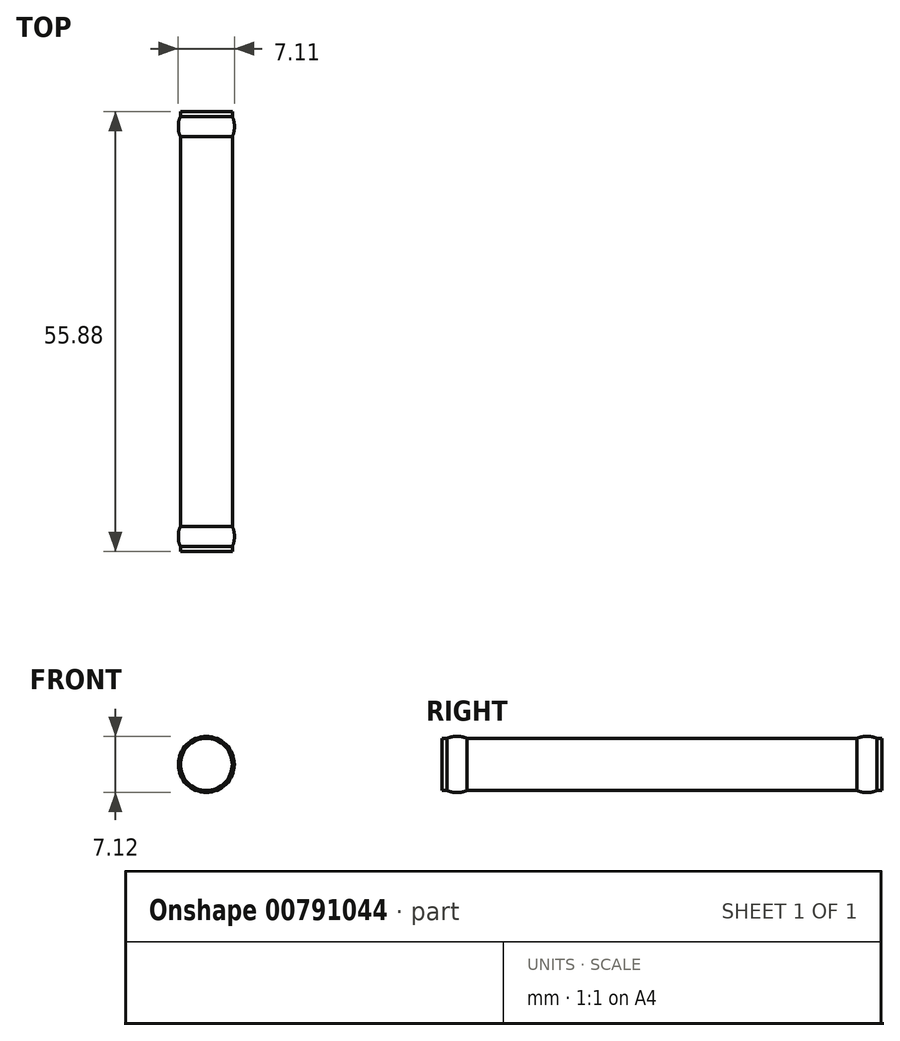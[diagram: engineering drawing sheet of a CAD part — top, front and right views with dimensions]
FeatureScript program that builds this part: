
annotation { "Feature Type Name" : "Feature", "Feature Type Description" : "" }
export const myFeature = defineFeature(function(context is Context, id is Id, definition is map)
    precondition{}
    {
        {
            var Q0;
            Q0=qCreatedBy(makeId("Front.planeOp"),FACE);
            var sketch = newSketch(context, id + "F0", { "sketchPlane" : qUnion([Q0])});
            skCircle(sketch, "E0", {"center": v(-16, 0) * mm, "radius": 3.3 * mm});
            skLineSegment(sketch, "E1", {"start": v(-12.7, 0) * mm, "end": v(0, 0) * mm});
            skSolve(sketch);
        }
        {
            var Q0;
            Q0=makeQuery(id+"F0.imprint","IMPRINT",FACE,{"disambiguationData":[TD([[makeQuery(id+"F0.imprint","IMPRINT",EDGE,{"derivedFrom":sQuery(id+"F0.wireOp",EDGE,"E0")}),1.0]])]});
            var Q1;
            Q1=makeQuery(id+"F0.imprint","IMPRINT",FACE,{"disambiguationData":[TD([[makeQuery(id+"F0.imprint","IMPRINT",EDGE,{"derivedFrom":sQuery(id+"F0.wireOp",EDGE,"TjowqyiQ-MTEW-wuyz-Xt5a-qvUKrSVn7oxo")}),1.0]])]});
            extrude(context, id + "F1", {"entities" : qUnion([Q0, Q1]), "depth" : 55.88 * mm, "offsetDistance" : 25.4 * mm});
        }
        {
            var Q0;
            Q0=makeQuery(id+"F1.opExtrude","CAP_FACE",FACE,{"disambiguationData":[OSD([sQuery(id+"F0.wireOp",EDGE,"E0")])],"isStart":false});
            cPlane(context, id + "F2", {"entities" : qUnion([Q0]), "cplaneType" : CPlaneType.OFFSET, "offset" : 1.9 * mm, "oppositeDirection" : true, "width" : 152.4 * mm, "height" : 152.4 * mm});
        }
        {
            var Q0;
            Q0=qCreatedBy(id+"F2.planeOp",FACE);
            var sketch = newSketch(context, id + "F3", { "sketchPlane" : qUnion([Q0])});
            skCircle(sketch, "E2", {"center": v(-16, 0) * mm, "radius": 3.56 * mm});
            skSolve(sketch);
        }
        {
            var Q0;
            Q0=makeQuery(id+"F3.imprint","IMPRINT",FACE,{"disambiguationData":[TD([[makeQuery(id+"F3.imprint","IMPRINT",EDGE,{"derivedFrom":sQuery(id+"F3.wireOp",EDGE,"E2")}),1.0]])]});
            extrude(context, id + "F4", {"entities" : qUnion([Q0]), "endBound" : BoundingType.SYMMETRIC, "depth" : 2.54 * mm, "offsetDistance" : 25.4 * mm});
        }
        {
            var Q0;
            Q0=makeQuery(id+"F1.opExtrude","CAP_FACE",FACE,{"disambiguationData":[OSD([sQuery(id+"F0.wireOp",EDGE,"E0")])],"isStart":false});
            cPlane(context, id + "F5", {"entities" : qUnion([Q0]), "cplaneType" : CPlaneType.OFFSET, "offset" : 27.94 * mm, "oppositeDirection" : true, "width" : 152.4 * mm, "height" : 152.4 * mm});
        }
        {
            var Q0;
            Q0=makeQuery(id+"F4.opExtrude","SWEPT_BODY",BODY,{"disambiguationData":[OSD([sQuery(id+"F3.wireOp",EDGE,"E2")])]});
            var Q1;
            Q1=qCreatedBy(id+"F5.planeOp",FACE);
            mirror(context, id + "F6", {"operationType" : NewBodyOperationType.ADD, "entities" : qUnion([Q0]), "mirrorPlane" : qUnion([Q1])});
        }
        {
            var Q0;
            Q0=makeQuery(id+"F4.opExtrude","CAP_EDGE",EDGE,{"disambiguationData":[OSD([sQuery(id+"F3.wireOp",EDGE,"E2")])],"isStart":false});
            var Q1;
            Q1=makeQuery(id+"F4.opExtrude","CAP_EDGE",EDGE,{"disambiguationData":[OSD([sQuery(id+"F3.wireOp",EDGE,"E2")])],"isStart":true});
            var Q2;
            Q2=makeQuery(id+"F6.opPattern","COPY",EDGE,{"derivedFrom":makeQuery(id+"F4.opExtrude","CAP_EDGE",EDGE,{"disambiguationData":[OSD([sQuery(id+"F3.wireOp",EDGE,"E2")])],"isStart":true}),"instanceName":"1"});
            var Q3;
            Q3=makeQuery(id+"F6.opPattern","COPY",EDGE,{"derivedFrom":makeQuery(id+"F4.opExtrude","CAP_EDGE",EDGE,{"disambiguationData":[OSD([sQuery(id+"F3.wireOp",EDGE,"E2")])],"isStart":false}),"instanceName":"1"});
            fillet(context, id + "F7", {"entities" : qUnion([Q0, Q1, Q2, Q3]), "radius" : 2.54 * mm, "tangentPropagation" : true, "allowEdgeOverflow" : false});
        }
    });
